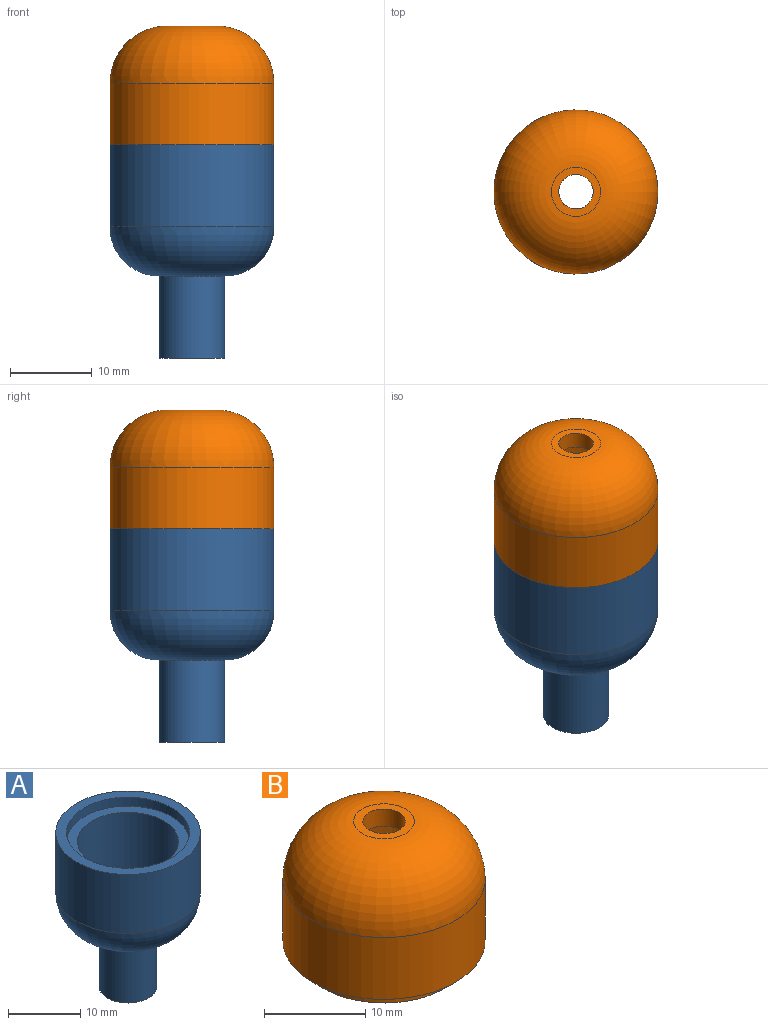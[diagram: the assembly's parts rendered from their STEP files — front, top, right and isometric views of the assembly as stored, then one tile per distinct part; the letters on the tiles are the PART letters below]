
ASSEMBLY  parts=2 mates=1
PART A: 10 faces, bbox 20x20x26 mm
  f0: cone r=0mm half-angle=59deg, axis (0,0,1), area 156.7mm2, adj f8,f9
  f1: plane 17x17mm, normal (0,0,1), area 73mm2, adj f7,f8
  f2: plane 8x8mm, normal (0,0,-1), area 30.6mm2, adj f3,f9
  f3: cylinder r=4mm len=10mm, axis (0,0,1), area 251.3mm2, adj f2,f4
  f4: torus R=4mm, axis (0,0,1), area 463.1mm2, adj f3,f5
  f5: cylinder r=10mm len=20mm, axis (0,0,1), area 628.3mm2, adj f4,f6
  f6: plane 20x20mm, normal (0,0,1), area 87.2mm2, adj f5,f7
  f7: cylinder r=8.5mm len=17mm, axis (0,0,1), area 80.1mm2, adj f1,f6
  f8: cylinder r=7mm len=14mm, axis (0,0,1), area 483.8mm2, adj f0,f1
  f9: cylinder r=2.5mm len=10.8mm, axis (0,0,-1), area 169.6mm2, adj f0,f2
PART B: 9 faces, bbox 20x20x16 mm
  f0: cone r=0mm half-angle=59deg, axis (0,0,-1), area 163.4mm2, adj f7,f8
  f1: plane 6x6mm, normal (0,0,1), area 14.4mm2, adj f6,f8
  f2: plane 17x17mm, normal (0,0,-1), area 73mm2, adj f3,f7
  f3: cylinder r=8.5mm len=17mm, axis (0,0,1), area 80.1mm2, adj f2,f4
  f4: plane 20x20mm, normal (0,0,-1), area 87.2mm2, adj f3,f5
  f5: cylinder r=10mm len=20mm, axis (0,0,1), area 471.2mm2, adj f4,f6
  f6: torus R=3mm, axis (0,0,1), area 515.1mm2, adj f1,f5
  f7: cylinder r=7mm len=14mm, axis (0,0,-1), area 483.8mm2, adj f0,f2
  f8: cylinder r=2.1mm len=4.2mm, axis (0,0,1), area 27.1mm2, adj f0,f1
PLACE A t=(3.02,2.6,-6.72)mm
PLACE B t=(3.02,2.6,-6.72)mm
MATE fastened A.f0 <-> B.f0  axis (0,0,1) through (3.02,2.6,-5.22)mm
